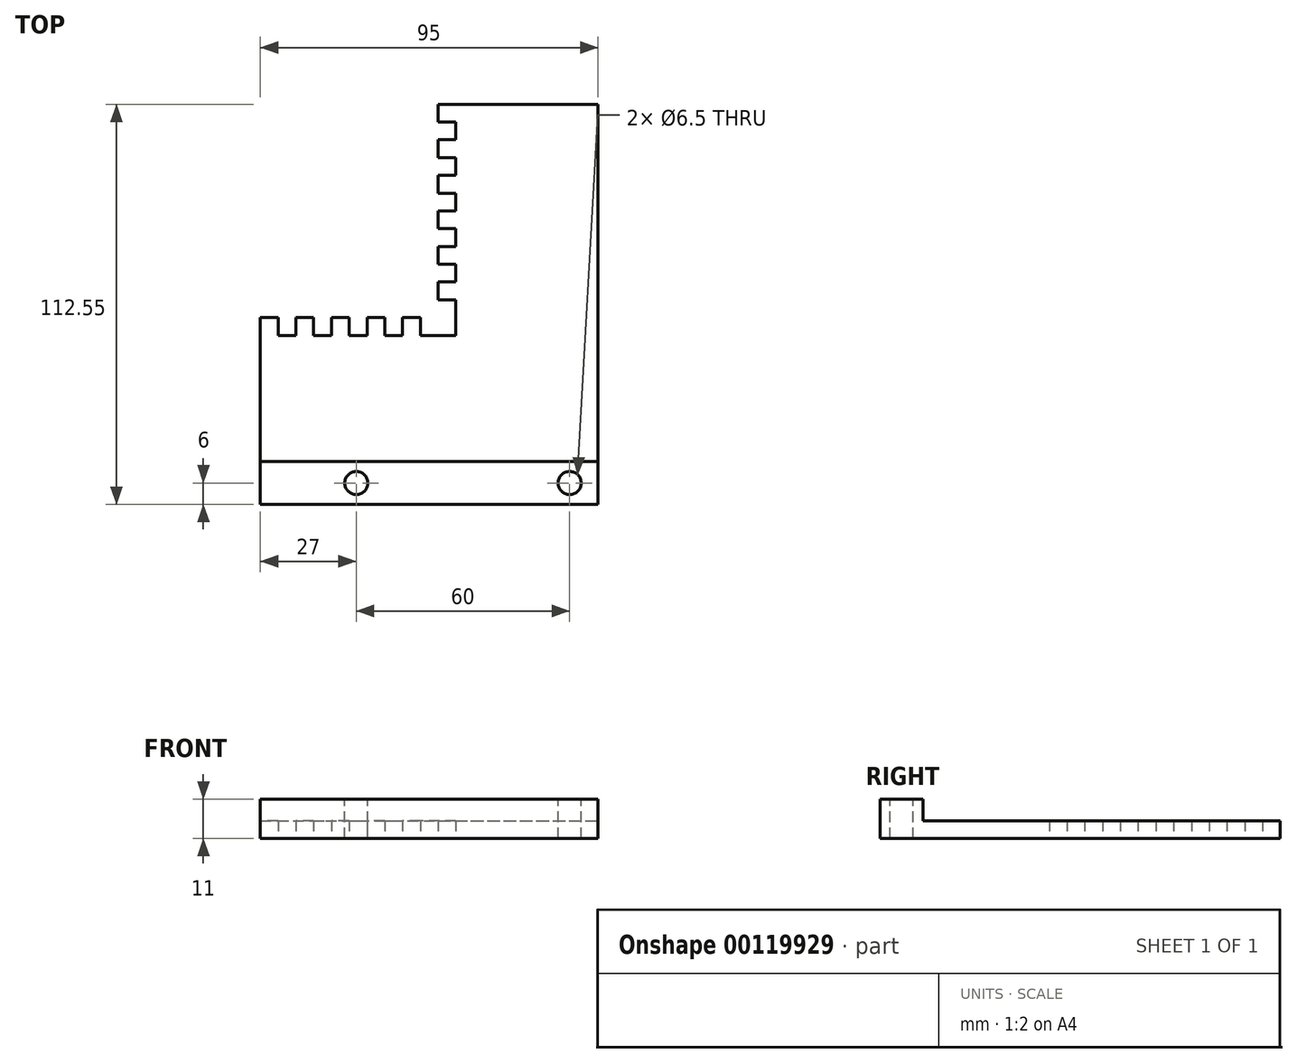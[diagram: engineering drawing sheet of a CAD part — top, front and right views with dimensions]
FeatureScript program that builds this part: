
annotation { "Feature Type Name" : "Feature", "Feature Type Description" : "" }
export const myFeature = defineFeature(function(context is Context, id is Id, definition is map)
    precondition{}
    {
        {
            var Q0;
            Q0=qCreatedBy(makeId("Top.planeOp"),FACE);
            var sketch = newSketch(context, id + "F0", { "sketchPlane" : qUnion([Q0])});
            skLineSegment(sketch, "E0.bottom", {"start": v(0, 0) * mm, "end": v(76, 0) * mm});
            skLineSegment(sketch, "E0.right", {"start": v(76, 0) * mm, "end": v(76, 55) * mm});
            skLineSegment(sketch, "E1", {"start": v(0, 12) * mm, "end": v(76, 12) * mm});
            skLineSegment(sketch, "E2.top", {"start": v(31, 112.55) * mm, "end": v(76, 112.55) * mm});
            skLineSegment(sketch, "E2.right", {"start": v(76, 52.55) * mm, "end": v(76, 112.55) * mm});
            skLineSegment(sketch, "E3.top", {"start": v(31, 57.55) * mm, "end": v(36, 57.55) * mm});
            skLineSegment(sketch, "E3.right", {"start": v(36, 52.55) * mm, "end": v(36, 57.55) * mm});
            skLineSegment(sketch, "E4.0.1.0", {"start": v(36, 62.55) * mm, "end": v(36, 67.55) * mm});
            skLineSegment(sketch, "E4.0.1.1", {"start": v(31, 67.55) * mm, "end": v(36, 67.55) * mm});
            skLineSegment(sketch, "E4.0.1.3", {"start": v(31, 62.55) * mm, "end": v(36, 62.55) * mm});
            skLineSegment(sketch, "E4.0.2.0", {"start": v(36, 72.55) * mm, "end": v(36, 77.55) * mm});
            skLineSegment(sketch, "E4.0.2.1", {"start": v(31, 77.55) * mm, "end": v(36, 77.55) * mm});
            skLineSegment(sketch, "E4.0.2.3", {"start": v(31, 72.55) * mm, "end": v(36, 72.55) * mm});
            skLineSegment(sketch, "E4.0.3.0", {"start": v(36, 82.55) * mm, "end": v(36, 87.55) * mm});
            skLineSegment(sketch, "E4.0.3.1", {"start": v(31, 87.55) * mm, "end": v(36, 87.55) * mm});
            skLineSegment(sketch, "E4.0.3.3", {"start": v(31, 82.55) * mm, "end": v(36, 82.55) * mm});
            skLineSegment(sketch, "E4.0.4.0", {"start": v(36, 92.55) * mm, "end": v(36, 97.55) * mm});
            skLineSegment(sketch, "E4.0.4.1", {"start": v(31, 97.55) * mm, "end": v(36, 97.55) * mm});
            skLineSegment(sketch, "E4.0.4.3", {"start": v(31, 92.55) * mm, "end": v(36, 92.55) * mm});
            skLineSegment(sketch, "E4.0.5.0", {"start": v(36, 102.55) * mm, "end": v(36, 107.55) * mm});
            skLineSegment(sketch, "E4.0.5.1", {"start": v(31, 107.55) * mm, "end": v(36, 107.55) * mm});
            skLineSegment(sketch, "E4.0.5.3", {"start": v(31, 102.55) * mm, "end": v(36, 102.55) * mm});
            skLineSegment(sketch, "E5", {"start": v(31, 112.55) * mm, "end": v(31, 107.55) * mm});
            skLineSegment(sketch, "E6", {"start": v(31, 102.55) * mm, "end": v(31, 97.55) * mm});
            skLineSegment(sketch, "E7", {"start": v(31, 92.55) * mm, "end": v(31, 87.55) * mm});
            skLineSegment(sketch, "E8", {"start": v(31, 82.55) * mm, "end": v(31, 77.55) * mm});
            skLineSegment(sketch, "E9", {"start": v(31, 72.55) * mm, "end": v(31, 67.55) * mm});
            skLineSegment(sketch, "E10", {"start": v(31, 62.55) * mm, "end": v(31, 57.55) * mm});
            skLineSegment(sketch, "E11.top", {"start": v(-19, 52.55) * mm, "end": v(-19, 47.55) * mm});
            skLineSegment(sketch, "E12.0.1.0", {"start": v(-14, 47.55) * mm, "end": v(-9, 47.55) * mm});
            skLineSegment(sketch, "E12.0.1.1", {"start": v(-9, 52.55) * mm, "end": v(-9, 47.55) * mm});
            skLineSegment(sketch, "E12.0.1.3", {"start": v(-14, 52.55) * mm, "end": v(-14, 47.55) * mm});
            skLineSegment(sketch, "E12.0.2.0", {"start": v(-4, 47.55) * mm, "end": v(1, 47.55) * mm});
            skLineSegment(sketch, "E12.0.2.1", {"start": v(1, 52.55) * mm, "end": v(1, 47.55) * mm});
            skLineSegment(sketch, "E12.0.2.3", {"start": v(-4, 52.55) * mm, "end": v(-4, 47.55) * mm});
            skLineSegment(sketch, "E12.0.3.0", {"start": v(6, 47.55) * mm, "end": v(11, 47.55) * mm});
            skLineSegment(sketch, "E12.0.3.1", {"start": v(11, 52.55) * mm, "end": v(11, 47.55) * mm});
            skLineSegment(sketch, "E12.0.3.3", {"start": v(6, 52.55) * mm, "end": v(6, 47.55) * mm});
            skLineSegment(sketch, "E12.0.4.0", {"start": v(16, 47.55) * mm, "end": v(21, 47.55) * mm});
            skLineSegment(sketch, "E12.0.4.1", {"start": v(21, 52.55) * mm, "end": v(21, 47.55) * mm});
            skLineSegment(sketch, "E12.0.4.3", {"start": v(16, 52.55) * mm, "end": v(16, 47.55) * mm});
            skLineSegment(sketch, "E12.0.5.3", {"start": v(26, 52.55) * mm, "end": v(26, 47.55) * mm});
            skLineSegment(sketch, "E13", {"start": v(26, 52.55) * mm, "end": v(21, 52.55) * mm});
            skLineSegment(sketch, "E14", {"start": v(16, 52.55) * mm, "end": v(11, 52.55) * mm});
            skLineSegment(sketch, "E15", {"start": v(6, 52.55) * mm, "end": v(1, 52.55) * mm});
            skLineSegment(sketch, "E16", {"start": v(-4, 52.55) * mm, "end": v(-9, 52.55) * mm});
            skLineSegment(sketch, "E17", {"start": v(-14, 52.55) * mm, "end": v(-19, 52.55) * mm});
            skLineSegment(sketch, "E18", {"start": v(36, 57.55) * mm, "end": v(36, 47.55) * mm});
            skLineSegment(sketch, "E19", {"start": v(36, 47.55) * mm, "end": v(26, 47.55) * mm});
            skLineSegment(sketch, "E20", {"start": v(-19, 47.55) * mm, "end": v(-19, 0) * mm});
            skLineSegment(sketch, "E21", {"start": v(0, 0) * mm, "end": v(-19, 0) * mm});
            skLineSegment(sketch, "E22", {"start": v(0, 12) * mm, "end": v(-19, 12) * mm});
            skSolve(sketch);
        }
        {
            var Q0;
            {var subQ0=sQuery(id+"F0.wireOp",EDGE,"E0.bottom");Q0=makeQuery(id+"F0.imprint","IMPRINT",FACE,{"disambiguationData":[TD([[makeQuery(id+"F0.imprint","IMPRINT",EDGE,{"derivedFrom":subQ0}),1.0]])]});}
            extrude(context, id + "F1", {"entities" : qUnion([Q0]), "depth" : 11 * mm});
        }
        {
            var Q0;
            Q0=makeQuery(id+"F1.opExtrude","CAP_FACE",FACE,{"disambiguationData":[OSD([sQuery(id+"F0.wireOp",EDGE,"E0.bottom"),sQuery(id+"F0.wireOp",EDGE,"E0.left"),sQuery(id+"F0.wireOp",EDGE,"E0.right"),sQuery(id+"F0.wireOp",EDGE,"E1")])],"isStart":false});
            var sketch = newSketch(context, id + "F2", { "sketchPlane" : qUnion([Q0])});
            skCircle(sketch, "E23", {"center": v(8, 6) * mm, "radius": 3.25 * mm});
            skCircle(sketch, "E24", {"center": v(68, 6) * mm, "radius": 3.25 * mm});
            skSolve(sketch);
        }
        {
            var Q0;
            Q0=sQuery(id+"F2.wireOp",VERTEX,"E23.center");
            var Q1;
            Q1=makeQuery(id+"F1.opExtrude","SWEPT_BODY",BODY,{"disambiguationData":[OSD([sQuery(id+"F0.wireOp",EDGE,"E0.bottom"),sQuery(id+"F0.wireOp",EDGE,"E0.left"),sQuery(id+"F0.wireOp",EDGE,"E0.right"),sQuery(id+"F0.wireOp",EDGE,"E1")])]});
            hole(context, id + "F3", {"style" : HoleStyle.SIMPLE, "endStyle" : HoleEndStyle.THROUGH, "holeDiameter" : 6.5 * mm, "locations" : qUnion([Q0]), "scope" : qUnion([Q1]), "isTappedThrough" : true});
        }
        {
            var Q0;
            Q0=sQuery(id+"F2.wireOp",VERTEX,"E24.center");
            var Q1;
            Q1=makeQuery(id+"F1.opExtrude","SWEPT_BODY",BODY,{"disambiguationData":[OSD([sQuery(id+"F0.wireOp",EDGE,"E0.bottom"),sQuery(id+"F0.wireOp",EDGE,"E0.left"),sQuery(id+"F0.wireOp",EDGE,"E0.right"),sQuery(id+"F0.wireOp",EDGE,"E1")])]});
            hole(context, id + "F4", {"style" : HoleStyle.SIMPLE, "endStyle" : HoleEndStyle.THROUGH, "holeDiameter" : 6.5 * mm, "locations" : qUnion([Q0]), "scope" : qUnion([Q1]), "isTappedThrough" : true});
        }
        {
            var Q0;
            {var subQ8=sQuery(id+"F0.wireOp",EDGE,"E1");Q0=makeQuery(id+"F0.imprint","IMPRINT",FACE,{"disambiguationData":[TD([[makeQuery(id+"F0.imprint","IMPRINT",EDGE,{"derivedFrom":subQ8}),1.0]])]});}
            extrude(context, id + "F5", {"entities" : qUnion([Q0]), "operationType" : NewBodyOperationType.ADD, "depth" : 5 * mm});
        }
    });
